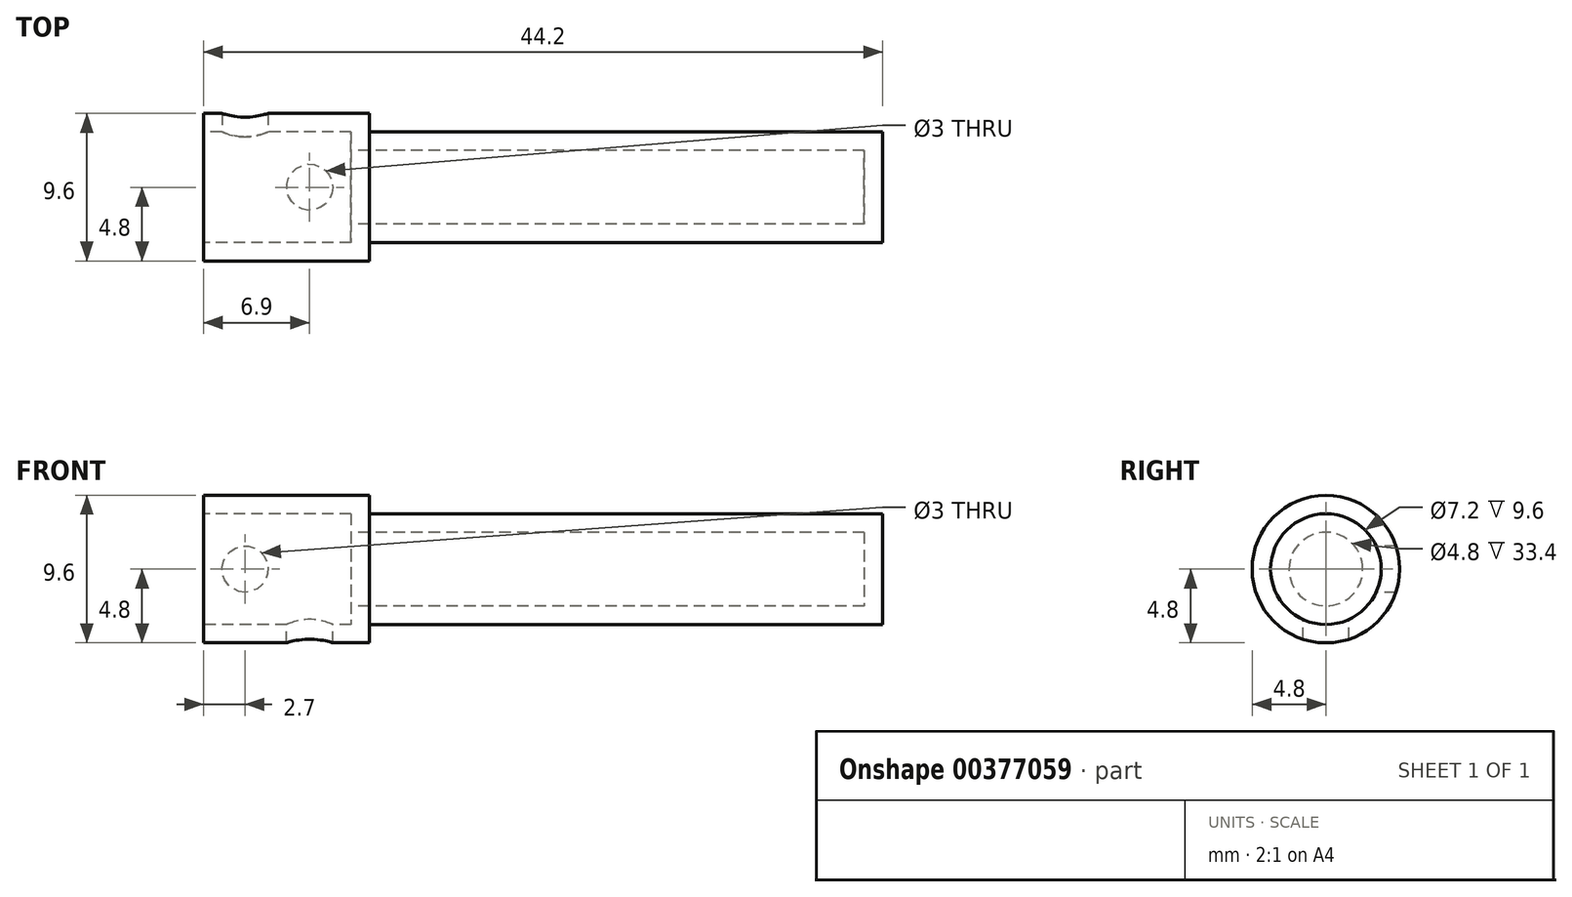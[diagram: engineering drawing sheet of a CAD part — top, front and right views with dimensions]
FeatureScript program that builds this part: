
annotation { "Feature Type Name" : "Feature", "Feature Type Description" : "" }
export const myFeature = defineFeature(function(context is Context, id is Id, definition is map)
    precondition{}
    {
        {
            var Q0;
            Q0=qCreatedBy(makeId("Front.planeOp"),FACE);
            var sketch = newSketch(context, id + "F0", { "sketchPlane" : qUnion([Q0])});
            skLineSegment(sketch, "E0", {"start": v(0, 3.6) * mm, "end": v(9.6, 3.6) * mm});
            skLineSegment(sketch, "E1", {"start": v(9.6, 2.4) * mm, "end": v(18.6, 2.4) * mm});
            skLineSegment(sketch, "E2", {"start": v(0, 2.4) * mm, "end": v(-9, 2.4) * mm});
            skCircle(sketch, "E3", {"center": v(2.7, 0) * mm, "radius": 1.5 * mm});
            skCircle(sketch, "E4", {"center": v(6.9, 0) * mm, "radius": 1.5 * mm});
            skPoint(sketch, "E5", {"position": v(1.2, 0) * mm});
            skPoint(sketch, "E6", {"position": v(4.2, 0) * mm});
            skPoint(sketch, "E7", {"position": v(5.4, 0) * mm});
            skPoint(sketch, "E8", {"position": v(8.4, 0) * mm});
            skLineSegment(sketch, "E9", {"start": v(-11.37, 1.2) * mm, "end": v(-7.92, 1.2) * mm});
            skLineSegment(sketch, "E10.bottom", {"start": v(11.2, 4.6) * mm, "end": v(13.2, 4.6) * mm});
            skLineSegment(sketch, "E10.top", {"start": v(11.2, 3.6) * mm, "end": v(13.2, 3.6) * mm});
            skLineSegment(sketch, "E10.left", {"start": v(11.2, 4.6) * mm, "end": v(11.2, 3.6) * mm});
            skLineSegment(sketch, "E10.right", {"start": v(13.2, 4.6) * mm, "end": v(13.2, 3.6) * mm});
            skLineSegment(sketch, "E11.bottom", {"start": v(-3.6, 4.6) * mm, "end": v(-1.6, 4.6) * mm});
            skLineSegment(sketch, "E11.top", {"start": v(-3.6, 3.6) * mm, "end": v(-1.6, 3.6) * mm});
            skLineSegment(sketch, "E11.left", {"start": v(-3.6, 4.6) * mm, "end": v(-3.6, 3.6) * mm});
            skLineSegment(sketch, "E11.right", {"start": v(-1.6, 4.6) * mm, "end": v(-1.6, 3.6) * mm});
            skLineSegment(sketch, "E12", {"start": v(9.6, 3.6) * mm, "end": v(11.2, 3.6) * mm, "construction": true});
            skLineSegment(sketch, "E13", {"start": v(0, 3.6) * mm, "end": v(-1.6, 3.6) * mm, "construction": true});
            skLineSegment(sketch, "E14", {"start": v(-3.6, 4.6) * mm, "end": v(-1.6, 3.6) * mm});
            skLineSegment(sketch, "E15", {"start": v(-3.6, 3.6) * mm, "end": v(-1.6, 4.6) * mm});
            skLineSegment(sketch, "E16", {"start": v(13.2, 4.6) * mm, "end": v(11.2, 3.6) * mm});
            skLineSegment(sketch, "E17", {"start": v(11.2, 4.6) * mm, "end": v(13.2, 3.6) * mm});
            skLineSegment(sketch, "E18", {"start": v(18.6, 2.2) * mm, "end": v(43, 2.2) * mm});
            skSolve(sketch);
        }
        {
            var Q0;
            Q0=qCreatedBy(makeId("Front.planeOp"),FACE);
            var sketch = newSketch(context, id + "F1", { "sketchPlane" : qUnion([Q0])});
            skLineSegment(sketch, "E19", {"start": v(0, 3.6) * mm, "end": v(9.6, 3.6) * mm});
            skLineSegment(sketch, "E20", {"start": v(9.6, 3.6) * mm, "end": v(9.6, 2.4) * mm});
            skLineSegment(sketch, "E21", {"start": v(43, 2.4) * mm, "end": v(43, 0) * mm});
            skLineSegment(sketch, "E22.trimOffspring", {"start": v(9.6, 2.4) * mm, "end": v(18.6, 2.4) * mm});
            skLineSegment(sketch, "E23", {"start": v(0, 3.6) * mm, "end": v(0, 4.8) * mm});
            skLineSegment(sketch, "E24", {"start": v(0, 4.8) * mm, "end": v(10.8, 4.8) * mm});
            skLineSegment(sketch, "E25", {"start": v(10.8, 3.6) * mm, "end": v(18.6, 3.6) * mm});
            skLineSegment(sketch, "E26", {"start": v(44.2, 0) * mm, "end": v(44.2, 3.6) * mm});
            skLineSegment(sketch, "E27", {"start": v(43, 0) * mm, "end": v(44.2, 0) * mm});
            skLineSegment(sketch, "E28", {"start": v(44.2, 3.6) * mm, "end": v(18.6, 3.6) * mm});
            skLineSegment(sketch, "E29", {"start": v(10.8, 4.8) * mm, "end": v(10.8, 3.6) * mm});
            skLineSegment(sketch, "E30", {"start": v(18.6, 2.4) * mm, "end": v(43, 2.4) * mm});
            skSolve(sketch);
        }
        {
            var Q0;
            Q0 = qSketchRegion(id + "F1", true);
            var Q1;
            Q1=sQuery(id+"F1.wireOp",EDGE,"E27");
            revolve(context, id + "F2", {"entities" : qUnion([Q0]), "axis" : qUnion([Q1]), "revolveType" : RevolveType.FULL});
        }
        {
            var Q0;
            Q0=qCreatedBy(makeId("Front.planeOp"),FACE);
            var sketch = newSketch(context, id + "F3", { "sketchPlane" : qUnion([Q0])});
            skCircle(sketch, "E31", {"center": v(2.7, 0) * mm, "radius": 1.5 * mm});
            skSolve(sketch);
        }
        {
            var Q0;
            Q0=qCreatedBy(makeId("Top.planeOp"),FACE);
            var sketch = newSketch(context, id + "F4", { "sketchPlane" : qUnion([Q0])});
            skCircle(sketch, "E32", {"center": v(6.9, 0) * mm, "radius": 1.5 * mm});
            skSolve(sketch);
        }
        {
            var Q0;
            Q0 = qSketchRegion(id + "F3", true);
            extrude(context, id + "F5", {"entities" : qUnion([Q0]), "operationType" : NewBodyOperationType.REMOVE, "endBound" : BoundingType.THROUGH_ALL, "oppositeDirection" : true, "depth" : 25 * mm});
        }
        {
            var Q0;
            Q0 = qSketchRegion(id + "F4", true);
            extrude(context, id + "F6", {"entities" : qUnion([Q0]), "operationType" : NewBodyOperationType.REMOVE, "endBound" : BoundingType.THROUGH_ALL, "oppositeDirection" : true, "depth" : 25 * mm});
        }
    });
